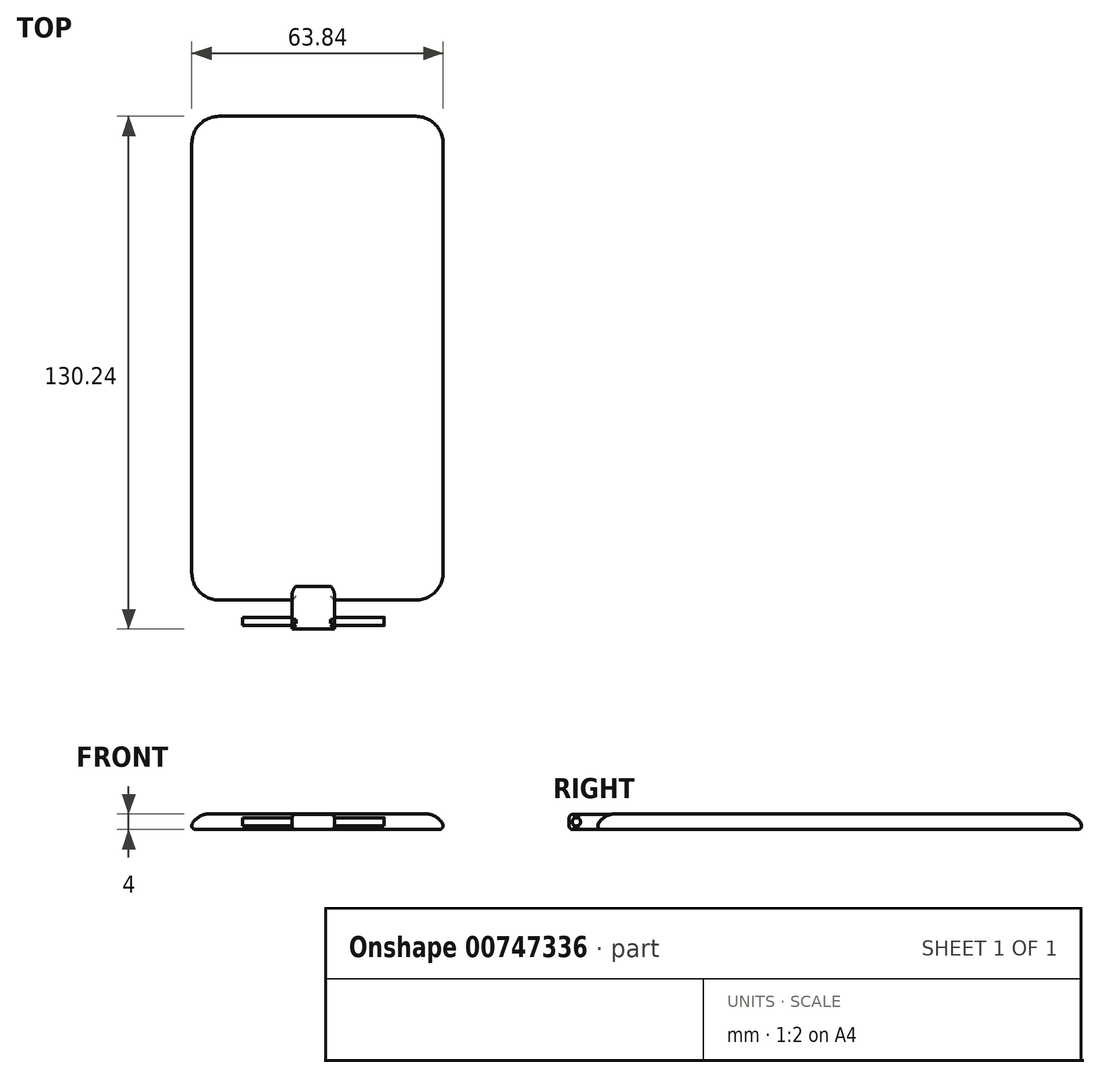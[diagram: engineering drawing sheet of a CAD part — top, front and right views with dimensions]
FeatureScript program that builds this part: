
annotation { "Feature Type Name" : "Feature", "Feature Type Description" : "" }
export const myFeature = defineFeature(function(context is Context, id is Id, definition is map)
    precondition{}
    {
        {
            var Q0;
            Q0=qCreatedBy(makeId("Top.planeOp"),FACE);
            var sketch = newSketch(context, id + "F0", { "sketchPlane" : qUnion([Q0])});
            skLineSegment(sketch, "E0.bottom", {"start": v(-23.95, 123.9) * mm, "end": v(26.05, 123.9) * mm});
            skLineSegment(sketch, "E0.top", {"start": v(-23.95, 0.1) * mm, "end": v(26.05, 0.1) * mm});
            skLineSegment(sketch, "E0.left", {"start": v(-31.3, 116.55) * mm, "end": v(-31.3, 7.45) * mm});
            skLineSegment(sketch, "E0.right", {"start": v(33.4, 116.55) * mm, "end": v(33.4, 7.45) * mm});
            skPoint(sketch, "E1.visualSharp", {"position": v(-32.3, 61.9) * mm});
            skArc(sketch, "E1.filletArc", {"start": v(-23.95, 123.9) * mm, "mid": v(-29.15, 121.75) * mm, "end": v(-31.3, 116.55) * mm});
            skPoint(sketch, "E2.visualSharp", {"position": v(26.3, 61.9) * mm});
            skArc(sketch, "E2.filletArc", {"start": v(33.4, 116.55) * mm, "mid": v(31.25, 121.75) * mm, "end": v(26.05, 123.9) * mm});
            skPoint(sketch, "E3.visualSharp", {"position": v(26.3, -61.9) * mm});
            skArc(sketch, "E3.filletArc", {"start": v(26.05, 0.1) * mm, "mid": v(31.25, 2.25) * mm, "end": v(33.4, 7.45) * mm});
            skPoint(sketch, "E4.visualSharp", {"position": v(-32.3, -61.9) * mm});
            skArc(sketch, "E4.filletArc", {"start": v(-31.3, 7.45) * mm, "mid": v(-29.15, 2.25) * mm, "end": v(-23.95, 0.1) * mm});
            skSolve(sketch);
        }
        {
            var Q0;
            Q0=makeQuery(id+"F0.imprint","IMPRINT",FACE,{"disambiguationData":[TD([[makeQuery(id+"F0.imprint","IMPRINT",EDGE,{"derivedFrom":sQuery(id+"F0.wireOp",EDGE,"E0.bottom")}),-1.0]])]});
            extrude(context, id + "F1", {"entities" : qUnion([Q0]), "depth" : 4 * mm, "offsetDistance" : 25 * mm});
        }
        {
            var Q0;
            Q0=makeQuery(id+"F1.opExtrude","CAP_EDGE",EDGE,{"disambiguationData":[OSD([sQuery(id+"F0.wireOp",EDGE,"E0.right")])],"isStart":false});
            fillet(context, id + "F2", {"entities" : qUnion([Q0]), "radius" : 5 * mm, "tangentPropagation" : true, "allowEdgeOverflow" : false});
        }
        {
            var Q0;
            Q0=makeQuery(id+"F1.opExtrude","CAP_FACE",FACE,{"disambiguationData":[OSD([sQuery(id+"F0.wireOp",EDGE,"E0.bottom"),sQuery(id+"F0.wireOp",EDGE,"E0.top"),sQuery(id+"F0.wireOp",EDGE,"E0.left"),sQuery(id+"F0.wireOp",EDGE,"E0.right"),sQuery(id+"F0.wireOp",EDGE,"E1.filletArc"),sQuery(id+"F0.wireOp",EDGE,"E2.filletArc"),sQuery(id+"F0.wireOp",EDGE,"E3.filletArc"),sQuery(id+"F0.wireOp",EDGE,"E4.filletArc")])],"isStart":true});
            fillet(context, id + "F3", {"entities" : qUnion([Q0]), "radius" : 1 * mm, "tangentPropagation" : true, "allowEdgeOverflow" : false});
        }
        {
            var Q0;
            Q0=qCreatedBy(makeId("Top.planeOp"),FACE);
            var sketch = newSketch(context, id + "F4", { "sketchPlane" : qUnion([Q0])});
            skLineSegment(sketch, "E5.bottom", {"start": v(5.4, -1.77) * mm, "end": v(-5.4, -1.77) * mm});
            skLineSegment(sketch, "E5.top", {"start": v(5.4, 1.77) * mm, "end": v(-5.4, 1.77) * mm});
            skLineSegment(sketch, "E5.left", {"start": v(5.4, -1.77) * mm, "end": v(5.4, 1.77) * mm});
            skLineSegment(sketch, "E5.right", {"start": v(-5.4, -1.77) * mm, "end": v(-5.4, 1.77) * mm});
            skPoint(sketch, "E5.middle", {"position": v(0, 0) * mm});
            skSolve(sketch);
        }
        {
            var Q0;
            Q0 = qSketchRegion(id + "F4", true);
            extrude(context, id + "F5", {"entities" : qUnion([Q0]), "operationType" : NewBodyOperationType.ADD, "depth" : 3.9 * mm, "offsetDistance" : 25 * mm});
        }
        {
            var Q0;
            Q0=makeQuery(id+"F5.opExtrude","SWEPT_FACE",FACE,{"disambiguationData":[OSD([sQuery(id+"F4.wireOp",EDGE,"E5.top")])]});
            extrude(context, id + "F6", {"entities" : qUnion([Q0]), "operationType" : NewBodyOperationType.ADD, "depth" : 4.8 * mm, "offsetDistance" : 25 * mm});
        }
        {
            var Q0;
            Q0=makeQuery(id+"F5.opExtrude","SWEPT_FACE",FACE,{"disambiguationData":[OSD([sQuery(id+"F4.wireOp",EDGE,"E5.bottom")])]});
            extrude(context, id + "F7", {"entities" : qUnion([Q0]), "operationType" : NewBodyOperationType.ADD, "depth" : 5 * mm, "offsetDistance" : 25 * mm});
        }
        {
            var Q0;
            Q0=qCreatedBy(makeId("Right.planeOp"),FACE);
            var sketch = newSketch(context, id + "F8", { "sketchPlane" : qUnion([Q0])});
            skCircle(sketch, "E6", {"center": v(-4.9, 1.97) * mm, "radius": 1.06 * mm});
            skSolve(sketch);
        }
        {
            var Q0;
            Q0 = qSketchRegion(id + "F8", true);
            extrude(context, id + "F9", {"entities" : qUnion([Q0]), "operationType" : NewBodyOperationType.ADD, "depth" : 18 * mm, "offsetDistance" : 25 * mm});
        }
        {
            var Q0;
            Q0 = qSketchRegion(id + "F8", true);
            extrude(context, id + "F10", {"entities" : qUnion([Q0]), "operationType" : NewBodyOperationType.ADD, "depth" : -18 * mm, "offsetDistance" : 25 * mm});
        }
        {
            var Q0;
            {var subQ0=sQuery(id+"F4.wireOp",EDGE,"E5.left");var subQ1=sQuery(id+"F4.wireOp",EDGE,"E5.bottom");Q0=makeQuery(id+"F7.boolean.opBoolean","MERGE",EDGE,{"derivedFrom":[makeQuery(id+"F6.boolean.opBoolean","MERGE",EDGE,{"derivedFrom":[makeQuery(id+"F5.opExtrude","CAP_EDGE",EDGE,{"disambiguationData":[OSD([subQ0])],"isStart":false}),makeQuery(id+"F6.opExtrude","SWEPT_EDGE",EDGE,{"disambiguationData":[OSD([sQuery(id+"F4.wireOp",EDGE,"E5.top"),subQ0])]})]}),makeQuery(id+"F7.opExtrude","SWEPT_EDGE",EDGE,{"disambiguationData":[OSD([subQ1,subQ0]),TDD([makeQuery(id+"F5.opExtrude","CAP_VERTEX",VERTEX,{"disambiguationData":[OSD([subQ1,subQ0])],"isStart":false})])]})]});}
            var Q1;
            {var subQ0=sQuery(id+"F4.wireOp",EDGE,"E5.right");var subQ1=sQuery(id+"F4.wireOp",EDGE,"E5.bottom");Q1=makeQuery(id+"F7.boolean.opBoolean","MERGE",EDGE,{"derivedFrom":[makeQuery(id+"F6.boolean.opBoolean","MERGE",EDGE,{"derivedFrom":[makeQuery(id+"F5.opExtrude","CAP_EDGE",EDGE,{"disambiguationData":[OSD([subQ0])],"isStart":false}),makeQuery(id+"F6.opExtrude","SWEPT_EDGE",EDGE,{"disambiguationData":[OSD([sQuery(id+"F4.wireOp",EDGE,"E5.top"),subQ0])]})]}),makeQuery(id+"F7.opExtrude","SWEPT_EDGE",EDGE,{"disambiguationData":[OSD([subQ1,subQ0]),TDD([makeQuery(id+"F5.opExtrude","CAP_VERTEX",VERTEX,{"disambiguationData":[OSD([subQ1,subQ0])],"isStart":false})])]})]});}
            var Q2;
            {var subQ0=sQuery(id+"F4.wireOp",EDGE,"E5.bottom");Q2=makeQuery(id+"F7.opExtrude","CAP_EDGE",EDGE,{"disambiguationData":[OSD([subQ0]),TDD([makeQuery(id+"F5.opExtrude","CAP_EDGE",EDGE,{"disambiguationData":[OSD([subQ0])],"isStart":false})])],"isStart":false});}
            var Q3;
            {var subQ0=sQuery(id+"F4.wireOp",EDGE,"E5.bottom");Q3=makeQuery(id+"F7.opExtrude","CAP_EDGE",EDGE,{"disambiguationData":[OSD([subQ0]),TDD([makeQuery(id+"F5.opExtrude","CAP_EDGE",EDGE,{"disambiguationData":[OSD([subQ0])],"isStart":true})])],"isStart":false});}
            var Q4;
            {var subQ0=sQuery(id+"F4.wireOp",EDGE,"E5.left");var subQ1=sQuery(id+"F4.wireOp",EDGE,"E5.bottom");Q4=makeQuery(id+"F7.boolean.opBoolean","MERGE",EDGE,{"derivedFrom":[makeQuery(id+"F5.opExtrude","CAP_EDGE",EDGE,{"disambiguationData":[OSD([subQ0])],"isStart":true}),makeQuery(id+"F7.opExtrude","SWEPT_EDGE",EDGE,{"disambiguationData":[OSD([subQ1,subQ0]),TDD([makeQuery(id+"F5.opExtrude","CAP_VERTEX",VERTEX,{"disambiguationData":[OSD([subQ1,subQ0])],"isStart":true})])]})]});}
            var Q5;
            {var subQ0=sQuery(id+"F4.wireOp",EDGE,"E5.right");var subQ1=sQuery(id+"F4.wireOp",EDGE,"E5.bottom");Q5=makeQuery(id+"F7.boolean.opBoolean","MERGE",EDGE,{"derivedFrom":[makeQuery(id+"F5.opExtrude","CAP_EDGE",EDGE,{"disambiguationData":[OSD([subQ0])],"isStart":true}),makeQuery(id+"F7.opExtrude","SWEPT_EDGE",EDGE,{"disambiguationData":[OSD([subQ1,subQ0]),TDD([makeQuery(id+"F5.opExtrude","CAP_VERTEX",VERTEX,{"disambiguationData":[OSD([subQ1,subQ0])],"isStart":true})])]})]});}
            fillet(context, id + "F11", {"entities" : qUnion([Q0, Q1, Q2, Q3, Q4, Q5]), "radius" : 1 * mm, "tangentPropagation" : true, "allowEdgeOverflow" : false});
        }
    });
